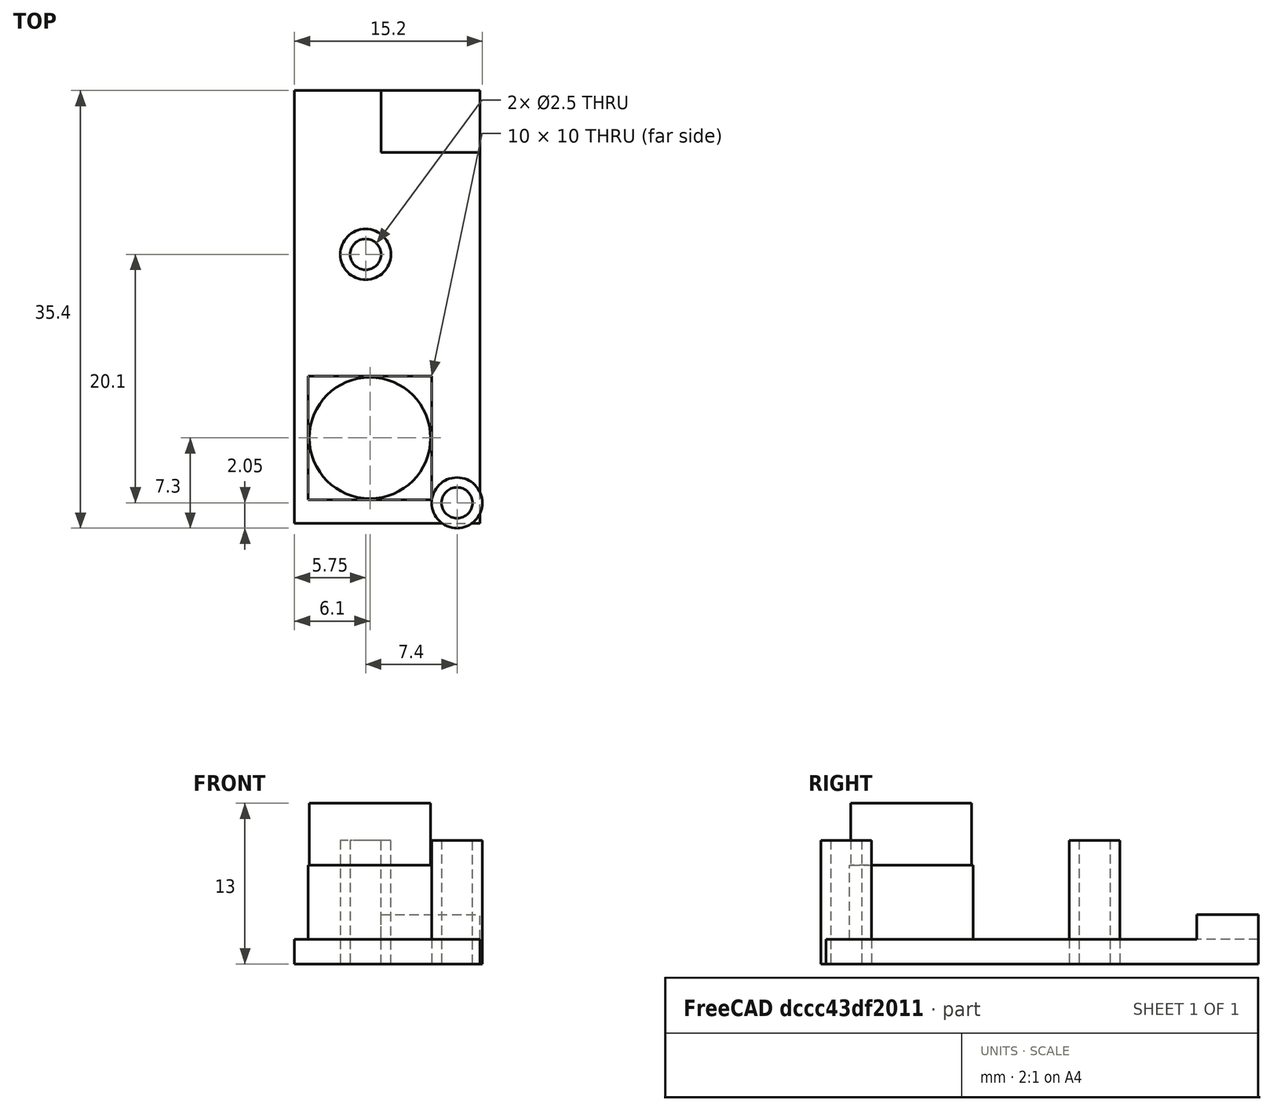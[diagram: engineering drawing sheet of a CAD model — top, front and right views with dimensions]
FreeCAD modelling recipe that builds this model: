
FCSTD DOCUMENT  (FreeCAD 1.0R1.0.1)
Label: Unknown_USB_Model_001
License: All rights reserved
LicenseURL: http://en.wikipedia.org/wiki/All_rights_reserved
objects: Part::Cylinder×7, Part::MultiFuse×4, Part::Box×3, Part::Cut×1
note: 15 computed .brp shape members not serialized (recipe doc carries the construction recipe); baked Part::Feature solids carry a one-line shape summary decoded from their .brp

FEATURE [Part::Box] Box  label="Cube"
  AttacherType = Attacher::AttachEngine3D
  Height = 2
  Length = 15
  Width = 35
FEATURE [Part::Box] Box001  label="Cube001"
  AttacherType = Attacher::AttachEngine3D
  Height = 8
  Length = 10
  Placement = pos=(1.1,1.9,0) rot=(0,0,1;0rad)
  Width = 10
FEATURE [Part::Cylinder] Cylinder
  Angle = 360
  AttacherType = Attacher::AttachEngine3D
  FirstAngle = 0
  Height = 13
  Placement = pos=(6.1,6.9,0) rot=(0,0,1;0rad)
  Radius = 4.9
  SecondAngle = 0
FEATURE [Part::Cylinder] Cylinder001
  Angle = 360
  AttacherType = Attacher::AttachEngine3D
  FirstAngle = 0
  Height = 10
  Placement = pos=(5.75,21.75,0) rot=(0,0,1;0rad)
  Radius = 1.25
  SecondAngle = 0
FEATURE [Part::Cylinder] Cylinder002
  Angle = 360
  AttacherType = Attacher::AttachEngine3D
  FirstAngle = 0
  Height = 10
  Placement = pos=(13.15,1.65,0) rot=(0,0,1;0rad)
  Radius = 1.25
  SecondAngle = 0
FEATURE [Part::Box] Box002  label="Cube002"
  AttacherType = Attacher::AttachEngine3D
  Height = 4
  Length = 8
  Placement = pos=(7,30,0) rot=(0,0,1;0rad)
  Width = 5
FEATURE [Part::MultiFuse] Fusion  label="BaseBodyTemplate"
  Shapes = -> [Box002,Box,Box001,Cylinder]
FEATURE [Part::MultiFuse] Fusion001  label="ScrewHoles"
  Shapes = -> [Cylinder002,Cylinder001]
FEATURE [Part::Cut] Cut  label="ModelWithHoles"
  Base = -> Fusion
  Tool = -> Fusion001
FEATURE [Part::Cylinder] Cylinder003
  Angle = 360
  AttacherType = Attacher::AttachEngine3D
  FirstAngle = 0
  Height = 10
  Placement = pos=(5.75,21.75,0) rot=(0,0,1;0rad)
  Radius = 1.25
  SecondAngle = 0
FEATURE [Part::Cylinder] Cylinder004
  Angle = 360
  AttacherType = Attacher::AttachEngine3D
  FirstAngle = 0
  Height = 10
  Placement = pos=(13.15,1.65,0) rot=(0,0,1;0rad)
  Radius = 1.25
  SecondAngle = 0
FEATURE [Part::MultiFuse] Fusion002  label="ScrewTemplates_Through"
  Shapes = -> [Cylinder004,Cylinder003]
FEATURE [Part::Cylinder] Cylinder005
  Angle = 360
  AttacherType = Attacher::AttachEngine3D
  FirstAngle = 0
  Height = 10
  Placement = pos=(5.75,21.75,0) rot=(0,0,1;0rad)
  Radius = 2.05
  SecondAngle = 0
FEATURE [Part::Cylinder] Cylinder006
  Angle = 360
  AttacherType = Attacher::AttachEngine3D
  FirstAngle = 0
  Height = 10
  Placement = pos=(13.15,1.65,0) rot=(0,0,1;0rad)
  Radius = 2.05
  SecondAngle = 0
FEATURE [Part::MultiFuse] Fusion003  label="ScrewTemplates_Core"
  Shapes = -> [Cylinder006,Cylinder005]
